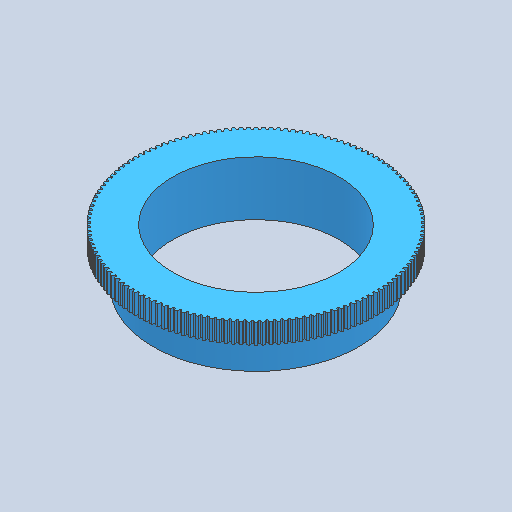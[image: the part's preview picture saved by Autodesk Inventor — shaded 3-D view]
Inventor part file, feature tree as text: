
AUTODESK INVENTOR PART (.ipt)
format: ipt  version: 2023 (Build 270158030, 158C)  size: 1,042,944 bytes
history: native  units: mm
features: extrude x4, sketch x4, other x1
ambient origin geometry x8: Origin, YZ Plane, XZ Plane, XY Plane, X Axis, Y Axis, Z Axis, Center Point
bodies: Body1 (feature_tree)
feature tree (9):
  other  "ソリッド1"
  extrude  "押し出し1"  Depth=15.5mm
  extrude  "押し出し2"  Depth=2.6mm TaperAngle=0.0deg
  extrude  "押し出し3"  Depth=18.0mm
  extrude  "押し出し4"  Depth=1.5mm TaperAngle=0.0deg
  sketch  "スケッチ1"
  sketch  "スケッチ2"
  sketch  "スケッチ3"
  sketch  "スケッチ4"
